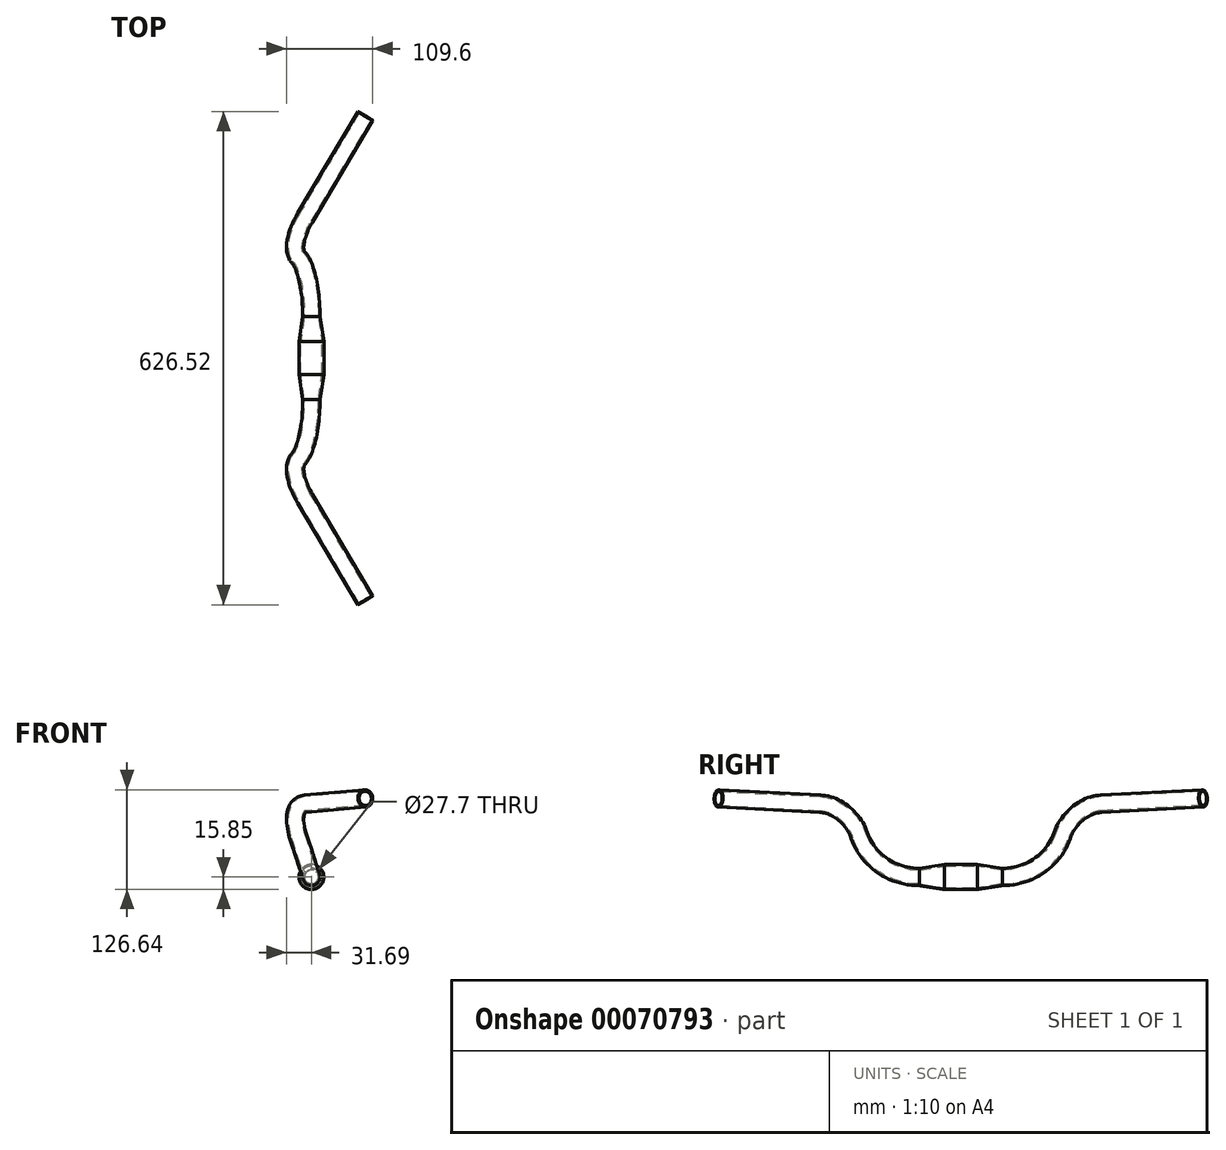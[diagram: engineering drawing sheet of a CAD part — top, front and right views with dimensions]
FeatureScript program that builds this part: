
annotation { "Feature Type Name" : "Feature", "Feature Type Description" : "" }
export const myFeature = defineFeature(function(context is Context, id is Id, definition is map)
    precondition{}
    {
        {
            var Q0;
            Q0=qCreatedBy(makeId("Front.planeOp"),FACE);
            var sketch = newSketch(context, id + "F0", { "sketchPlane" : qUnion([Q0])});
            skCircle(sketch, "E0", {"center": v(0, 0) * mm, "radius": 15.85 * mm});
            skSolve(sketch);
        }
        {
            var Q0;
            Q0 = qSketchRegion(id + "F0", true);
            extrude(context, id + "F1", {"entities" : qUnion([Q0]), "depth" : 21 * mm});
        }
        {
            var Q0;
            Q0=makeQuery(id+"F1.opExtrude","CAP_FACE",FACE,{"disambiguationData":[OSD([sQuery(id+"F0.wireOp",EDGE,"E0")])],"isStart":false});
            cPlane(context, id + "F2", {"entities" : qUnion([Q0]), "cplaneType" : CPlaneType.OFFSET, "offset" : 31.7 * mm, "width" : 150 * mm, "height" : 150 * mm});
        }
        {
            var Q0;
            Q0=qCreatedBy(id+"F2.planeOp",FACE);
            var sketch = newSketch(context, id + "F3", { "sketchPlane" : qUnion([Q0])});
            skCircle(sketch, "E1", {"center": v(0, 0) * mm, "radius": 11 * mm});
            skSolve(sketch);
        }
        {
            var Q1;
            Q1=makeQuery(id+"F1.opExtrude","CAP_FACE",FACE,{"disambiguationData":[OSD([sQuery(id+"F0.wireOp",EDGE,"E0")])],"isStart":false});
            var Q2;
            Q2=makeQuery(id+"F3.imprint","IMPRINT",FACE,{"disambiguationData":[TD([[makeQuery(id+"F3.imprint","IMPRINT",EDGE,{"derivedFrom":sQuery(id+"F3.wireOp",EDGE,"E1")}),1.0]])]});
            loft(context, id + "F4", {"operationType" : NewBodyOperationType.ADD, "sheetProfilesArray" : [{ "sheetProfileEntities" : qUnion([Q1]) }, { "sheetProfileEntities" : qUnion([Q2]) }]});
        }
        {
            var Q0;
            Q0=makeQuery(id+"F4.opLoft","CAP_FACE",FACE,{"disambiguationData":[OSD([makeQuery(id+"F3.imprint","IMPRINT",FACE,{"disambiguationData":[TD([[makeQuery(id+"F3.imprint","IMPRINT",EDGE,{"derivedFrom":sQuery(id+"F3.wireOp",EDGE,"E1")}),1.0]])]})])],"isStart":true});
            var sketch = newSketch(context, id + "F5", { "sketchPlane" : qUnion([Q0])});
            skCircle(sketch, "E2", {"center": v(0, 0) * mm, "radius": 11 * mm});
            skLineSegment(sketch, "E3", {"start": v(-44.53, 69.65) * mm, "end": v(4.42, 85.55) * mm, "construction": true});
            skSolve(sketch);
        }
        {
            var Q0;
            Q0=makeQuery(id+"F5.imprint","IMPRINT",FACE,{"disambiguationData":[TD([[makeQuery(id+"F5.imprint","IMPRINT",EDGE,{"derivedFrom":sQuery(id+"F5.wireOp",EDGE,"E2")}),1.0]])]});
            var Q1;
            Q1=sQuery(id+"F5.wireOp",EDGE,"E3");
            var Q2;
            Q2=sQuery(id+"F5.wireOp",EDGE,"E3");
            revolve(context, id + "F6", {"operationType" : NewBodyOperationType.ADD, "entities" : qUnion([Q0]), "surfaceEntities" : qUnion([Q1]), "axis" : qUnion([Q2]), "revolveType" : RevolveType.ONE_DIRECTION, "oppositeDirection" : true, "angle" : 72 * degree});
        }
        {
            var Q0;
            Q0=makeQuery(id+"F6.opRevolve","CAP_FACE",FACE,{"disambiguationData":[OSD([sQuery(id+"F5.wireOp",EDGE,"E2")])],"isStart":false});
            var sketch = newSketch(context, id + "F7", { "sketchPlane" : qUnion([Q0])});
            skLineSegment(sketch, "E4", {"start": v(26.73, -154.9) * mm, "end": v(93.38, -106.48) * mm, "construction": true});
            skCircle(sketch, "E5.0", {"center": v(10.53, -104.87) * mm, "radius": 11 * mm});
            skLineSegment(sketch, "E6", {"start": v(10.53, -104.87) * mm, "end": v(10.53, -183.85) * mm, "construction": true});
            skSolve(sketch);
        }
        {
            var Q0;
            Q0=makeQuery(id+"F7.imprint","IMPRINT",FACE,{"disambiguationData":[TD([[makeQuery(id+"F7.imprint","IMPRINT",EDGE,{"derivedFrom":sQuery(id+"F7.wireOp",EDGE,"E5.0")}),1.0]])]});
            var Q1;
            Q1=sQuery(id+"F7.wireOp",EDGE,"E4");
            var Q2;
            Q2=sQuery(id+"F7.wireOp",EDGE,"E4");
            revolve(context, id + "F8", {"operationType" : NewBodyOperationType.ADD, "entities" : qUnion([Q0]), "surfaceEntities" : qUnion([Q1]), "axis" : qUnion([Q2]), "revolveType" : RevolveType.ONE_DIRECTION, "angle" : 81 * degree});
        }
        {
            var Q0;
            Q0=makeQuery(id+"F8.opRevolve","CAP_FACE",FACE,{"disambiguationData":[OSD([sQuery(id+"F7.wireOp",EDGE,"E5.0")])],"isStart":false});
            var sketch = newSketch(context, id + "F9", { "sketchPlane" : qUnion([Q0])});
            skCircle(sketch, "E7.0", {"center": v(-100.08, 83.72) * mm, "radius": 11 * mm});
            skSolve(sketch);
        }
        {
            var Q0;
            Q0 = qSketchRegion(id + "F9", true);
            extrude(context, id + "F10", {"entities" : qUnion([Q0]), "operationType" : NewBodyOperationType.ADD, "depth" : 150 * mm});
        }
        {
            var Q0;
            Q0=makeQuery(id+"F1.opExtrude","SWEPT_BODY",BODY,{"disambiguationData":[OSD([sQuery(id+"F0.wireOp",EDGE,"E0")])]});
            var Q1;
            Q1=qCreatedBy(makeId("Front.planeOp"),FACE);
            mirror(context, id + "F11", {"operationType" : NewBodyOperationType.ADD, "entities" : qUnion([Q0]), "mirrorPlane" : qUnion([Q1])});
        }
        {
            var Q0;
            Q0=makeQuery(id+"F11.opPattern","COPY",FACE,{"derivedFrom":makeQuery(id+"F10.opExtrude","CAP_FACE",FACE,{"disambiguationData":[OSD([sQuery(id+"F9.wireOp",EDGE,"E7.0")])],"isStart":false}),"instanceName":"1"});
            var Q1;
            Q1=makeQuery(id+"F10.opExtrude","CAP_FACE",FACE,{"disambiguationData":[OSD([sQuery(id+"F9.wireOp",EDGE,"E7.0")])],"isStart":false});
            shell(context, id + "F12", {"entities" : qUnion([Q0, Q1]), "thickness" : 2 * mm});
        }
    });
